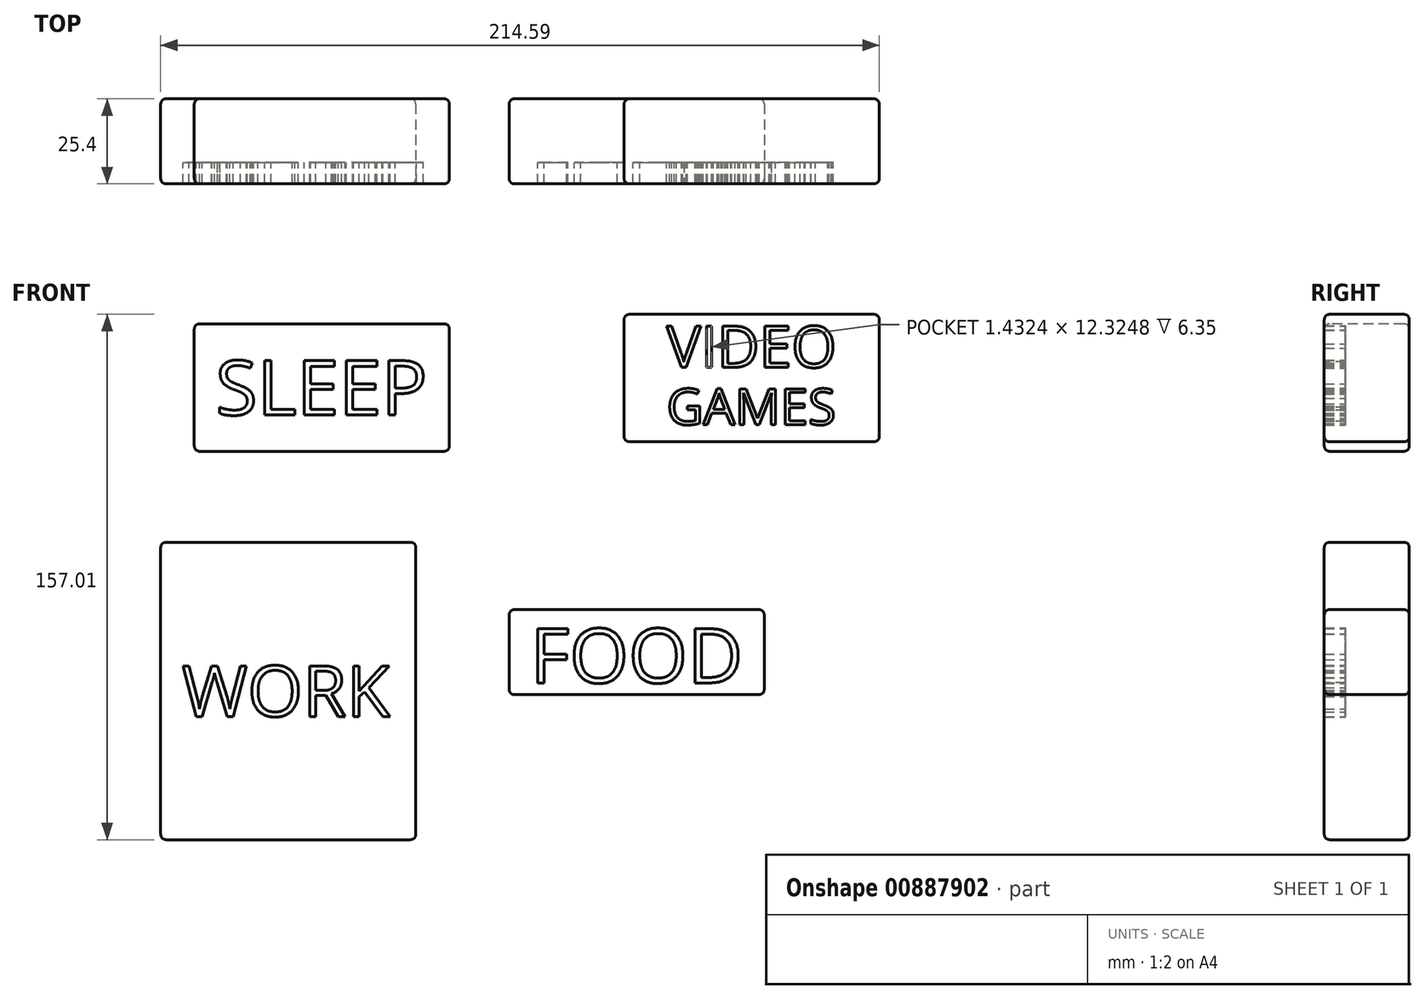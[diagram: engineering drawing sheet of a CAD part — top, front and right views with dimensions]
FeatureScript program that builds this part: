
annotation { "Feature Type Name" : "Feature", "Feature Type Description" : "" }
export const myFeature = defineFeature(function(context is Context, id is Id, definition is map)
    precondition{}
    {
        {
            var Q0;
            Q0=qCreatedBy(makeId("Front.planeOp"),FACE);
            var sketch = newSketch(context, id + "F0", { "sketchPlane" : qUnion([Q0])});
            skLineSegment(sketch, "E0.bottom", {"start": v(-75.08, 32.77) * mm, "end": v(1.12, 32.77) * mm});
            skLineSegment(sketch, "E0.top", {"start": v(-75.08, 70.87) * mm, "end": v(1.12, 70.87) * mm});
            skLineSegment(sketch, "E0.left", {"start": v(-75.08, 32.77) * mm, "end": v(-75.08, 70.87) * mm});
            skLineSegment(sketch, "E0.right", {"start": v(1.12, 32.77) * mm, "end": v(1.12, 70.87) * mm});
            skPoint(sketch, "E0.middle", {"position": v(-36.98, 51.82) * mm});
            skLineSegment(sketch, "E1.bottom", {"start": v(18.93, -39.95) * mm, "end": v(95.13, -39.95) * mm});
            skLineSegment(sketch, "E1.top", {"start": v(18.93, -14.55) * mm, "end": v(95.13, -14.55) * mm});
            skLineSegment(sketch, "E1.left", {"start": v(18.93, -39.95) * mm, "end": v(18.93, -14.55) * mm});
            skLineSegment(sketch, "E1.right", {"start": v(95.13, -39.95) * mm, "end": v(95.13, -14.55) * mm});
            skPoint(sketch, "E1.middle", {"position": v(57.03, -27.25) * mm});
            skLineSegment(sketch, "E2.bottom", {"start": v(-85.11, -83.3) * mm, "end": v(-8.91, -83.3) * mm});
            skLineSegment(sketch, "E2.top", {"start": v(-85.11, 5.6) * mm, "end": v(-8.91, 5.6) * mm});
            skLineSegment(sketch, "E2.left", {"start": v(-85.11, -83.3) * mm, "end": v(-85.11, 5.6) * mm});
            skLineSegment(sketch, "E2.right", {"start": v(-8.91, -83.3) * mm, "end": v(-8.91, 5.6) * mm});
            skPoint(sketch, "E2.middle", {"position": v(-47.01, -38.86) * mm});
            skLineSegment(sketch, "E3.bottom", {"start": v(129.48, 35.6) * mm, "end": v(53.28, 35.6) * mm});
            skLineSegment(sketch, "E3.top", {"start": v(129.48, 73.7) * mm, "end": v(53.28, 73.7) * mm});
            skLineSegment(sketch, "E3.left", {"start": v(129.48, 35.6) * mm, "end": v(129.48, 73.7) * mm});
            skLineSegment(sketch, "E3.right", {"start": v(53.28, 35.6) * mm, "end": v(53.28, 73.7) * mm});
            skPoint(sketch, "E3.middle", {"position": v(91.38, 54.65) * mm});
            skText(sketch, "E4", { "text": "WORK", "fontName": "OpenSans-Regular.ttf"});
            skText(sketch, "E5", { "text": "FOOD", "fontName": "OpenSans-Regular.ttf"});
            skText(sketch, "E6", { "text": "VIDEO", "fontName": "OpenSans-Regular.ttf"});
            skText(sketch, "E7", { "text": "GAMES", "fontName": "OpenSans-Regular.ttf"});
            skText(sketch, "E8", { "text": "SLEEP", "fontName": "OpenSans-Regular.ttf"});
            const initialGuessF0  = {"E4": [-0.07876, -0.04647, 1, 0, 0.01523], "E5": [0.02528, -0.03644, 1, 0, 0.0163], "E6": [0.06598, 0.05782, 1, 0, 0.01243], "E7": [0.06598, 0.04073, 1, 0, 0.0108], "E8": [-0.06873, 0.04364, 1, 0, 0.01635]};
            skSetInitialGuess(sketch, initialGuessF0);
            skSolve(sketch);
        }
        {
            var Q0;
            Q0 = qSketchRegion(id + "F0", true);
            var Q1;
            Q1=makeQuery(id+"F0.imprint","IMPRINT",FACE,{"disambiguationData":[TD([[makeQuery(id+"F0.imprint","IMPRINT",EDGE,{"derivedFrom":sQuery(id+"F0.wireOp",EDGE,"E8.sketch_text.stroke-55")}),-1.0]])]});
            var Q2;
            Q2=makeQuery(id+"F0.imprint","IMPRINT",FACE,{"disambiguationData":[TD([[makeQuery(id+"F0.imprint","IMPRINT",EDGE,{"derivedFrom":sQuery(id+"F0.wireOp",EDGE,"E8.sketch_text.stroke-31")}),-1.0]])]});
            var Q3;
            Q3=makeQuery(id+"F0.imprint","IMPRINT",FACE,{"disambiguationData":[TD([[makeQuery(id+"F0.imprint","IMPRINT",EDGE,{"derivedFrom":sQuery(id+"F0.wireOp",EDGE,"E8.sketch_text.stroke-43")}),-1.0]])]});
            var Q4;
            Q4=makeQuery(id+"F0.imprint","IMPRINT",FACE,{"disambiguationData":[TD([[makeQuery(id+"F0.imprint","IMPRINT",EDGE,{"derivedFrom":sQuery(id+"F0.wireOp",EDGE,"E8.sketch_text.stroke-63")}),1.0]])]});
            var Q5;
            Q5=makeQuery(id+"F0.imprint","IMPRINT",FACE,{"disambiguationData":[TD([[makeQuery(id+"F0.imprint","IMPRINT",EDGE,{"derivedFrom":sQuery(id+"F0.wireOp",EDGE,"E8.sketch_text.stroke-25")}),-1.0]])]});
            var Q6;
            Q6=makeQuery(id+"F0.imprint","IMPRINT",FACE,{"disambiguationData":[TD([[makeQuery(id+"F0.imprint","IMPRINT",EDGE,{"derivedFrom":sQuery(id+"F0.wireOp",EDGE,"E8.sketch_text.stroke-0")}),-1.0]])]});
            var Q7;
            Q7=makeQuery(id+"F0.imprint","IMPRINT",FACE,{"disambiguationData":[TD([[makeQuery(id+"F0.imprint","IMPRINT",EDGE,{"derivedFrom":sQuery(id+"F0.wireOp",EDGE,"E4.sketch_text.stroke-47")}),1.0]])]});
            var Q8;
            Q8=makeQuery(id+"F0.imprint","IMPRINT",FACE,{"disambiguationData":[TD([[makeQuery(id+"F0.imprint","IMPRINT",EDGE,{"derivedFrom":sQuery(id+"F0.wireOp",EDGE,"E4.sketch_text.stroke-36")}),-1.0]])]});
            var Q9;
            Q9=makeQuery(id+"F0.imprint","IMPRINT",FACE,{"disambiguationData":[TD([[makeQuery(id+"F0.imprint","IMPRINT",EDGE,{"derivedFrom":sQuery(id+"F0.wireOp",EDGE,"E4.sketch_text.stroke-54")}),-1.0]])]});
            var Q10;
            Q10=makeQuery(id+"F0.imprint","IMPRINT",FACE,{"disambiguationData":[TD([[makeQuery(id+"F0.imprint","IMPRINT",EDGE,{"derivedFrom":sQuery(id+"F0.wireOp",EDGE,"E4.sketch_text.stroke-20")}),-1.0]])]});
            var Q11;
            Q11=makeQuery(id+"F0.imprint","IMPRINT",FACE,{"disambiguationData":[TD([[makeQuery(id+"F0.imprint","IMPRINT",EDGE,{"derivedFrom":sQuery(id+"F0.wireOp",EDGE,"E4.sketch_text.stroke-28")}),1.0]])]});
            var Q12;
            Q12=makeQuery(id+"F0.imprint","IMPRINT",FACE,{"disambiguationData":[TD([[makeQuery(id+"F0.imprint","IMPRINT",EDGE,{"derivedFrom":sQuery(id+"F0.wireOp",EDGE,"E4.sketch_text.stroke-0")}),-1.0]])]});
            var Q13;
            Q13=makeQuery(id+"F0.imprint","IMPRINT",FACE,{"disambiguationData":[TD([[makeQuery(id+"F0.imprint","IMPRINT",EDGE,{"derivedFrom":sQuery(id+"F0.wireOp",EDGE,"E5.sketch_text.stroke-0")}),-1.0]])]});
            var Q14;
            Q14=makeQuery(id+"F0.imprint","IMPRINT",FACE,{"disambiguationData":[TD([[makeQuery(id+"F0.imprint","IMPRINT",EDGE,{"derivedFrom":sQuery(id+"F0.wireOp",EDGE,"E5.sketch_text.stroke-10")}),-1.0]])]});
            var Q15;
            Q15=makeQuery(id+"F0.imprint","IMPRINT",FACE,{"disambiguationData":[TD([[makeQuery(id+"F0.imprint","IMPRINT",EDGE,{"derivedFrom":sQuery(id+"F0.wireOp",EDGE,"E5.sketch_text.stroke-18")}),1.0]])]});
            var Q16;
            Q16=makeQuery(id+"F0.imprint","IMPRINT",FACE,{"disambiguationData":[TD([[makeQuery(id+"F0.imprint","IMPRINT",EDGE,{"derivedFrom":sQuery(id+"F0.wireOp",EDGE,"E5.sketch_text.stroke-26")}),-1.0]])]});
            var Q17;
            Q17=makeQuery(id+"F0.imprint","IMPRINT",FACE,{"disambiguationData":[TD([[makeQuery(id+"F0.imprint","IMPRINT",EDGE,{"derivedFrom":sQuery(id+"F0.wireOp",EDGE,"E5.sketch_text.stroke-34")}),1.0]])]});
            var Q18;
            Q18=makeQuery(id+"F0.imprint","IMPRINT",FACE,{"disambiguationData":[TD([[makeQuery(id+"F0.imprint","IMPRINT",EDGE,{"derivedFrom":sQuery(id+"F0.wireOp",EDGE,"E5.sketch_text.stroke-42")}),-1.0]])]});
            var Q19;
            Q19=makeQuery(id+"F0.imprint","IMPRINT",FACE,{"disambiguationData":[TD([[makeQuery(id+"F0.imprint","IMPRINT",EDGE,{"derivedFrom":sQuery(id+"F0.wireOp",EDGE,"E5.sketch_text.stroke-49")}),1.0]])]});
            var Q20;
            Q20=makeQuery(id+"F0.imprint","IMPRINT",FACE,{"disambiguationData":[TD([[makeQuery(id+"F0.imprint","IMPRINT",EDGE,{"derivedFrom":sQuery(id+"F0.wireOp",EDGE,"E6.sketch_text.stroke-47")}),1.0]])]});
            var Q21;
            Q21=makeQuery(id+"F0.imprint","IMPRINT",FACE,{"disambiguationData":[TD([[makeQuery(id+"F0.imprint","IMPRINT",EDGE,{"derivedFrom":sQuery(id+"F0.wireOp",EDGE,"E6.sketch_text.stroke-39")}),-1.0]])]});
            var Q22;
            Q22=makeQuery(id+"F0.imprint","IMPRINT",FACE,{"disambiguationData":[TD([[makeQuery(id+"F0.imprint","IMPRINT",EDGE,{"derivedFrom":sQuery(id+"F0.wireOp",EDGE,"E6.sketch_text.stroke-27")}),-1.0]])]});
            var Q23;
            Q23=makeQuery(id+"F0.imprint","IMPRINT",FACE,{"disambiguationData":[TD([[makeQuery(id+"F0.imprint","IMPRINT",EDGE,{"derivedFrom":sQuery(id+"F0.wireOp",EDGE,"E6.sketch_text.stroke-20")}),1.0]])]});
            var Q24;
            Q24=makeQuery(id+"F0.imprint","IMPRINT",FACE,{"disambiguationData":[TD([[makeQuery(id+"F0.imprint","IMPRINT",EDGE,{"derivedFrom":sQuery(id+"F0.wireOp",EDGE,"E6.sketch_text.stroke-13")}),-1.0]])]});
            var Q25;
            Q25=makeQuery(id+"F0.imprint","IMPRINT",FACE,{"disambiguationData":[TD([[makeQuery(id+"F0.imprint","IMPRINT",EDGE,{"derivedFrom":sQuery(id+"F0.wireOp",EDGE,"E6.sketch_text.stroke-9")}),-1.0]])]});
            var Q26;
            Q26=makeQuery(id+"F0.imprint","IMPRINT",FACE,{"disambiguationData":[TD([[makeQuery(id+"F0.imprint","IMPRINT",EDGE,{"derivedFrom":sQuery(id+"F0.wireOp",EDGE,"E6.sketch_text.stroke-0")}),-1.0]])]});
            var Q27;
            Q27=makeQuery(id+"F0.imprint","IMPRINT",FACE,{"disambiguationData":[TD([[makeQuery(id+"F0.imprint","IMPRINT",EDGE,{"derivedFrom":sQuery(id+"F0.wireOp",EDGE,"E7.sketch_text.stroke-28")}),1.0]])]});
            var Q28;
            Q28=makeQuery(id+"F0.imprint","IMPRINT",FACE,{"disambiguationData":[TD([[makeQuery(id+"F0.imprint","IMPRINT",EDGE,{"derivedFrom":sQuery(id+"F0.wireOp",EDGE,"E7.sketch_text.stroke-0")}),-1.0]])]});
            var Q29;
            Q29=makeQuery(id+"F0.imprint","IMPRINT",FACE,{"disambiguationData":[TD([[makeQuery(id+"F0.imprint","IMPRINT",EDGE,{"derivedFrom":sQuery(id+"F0.wireOp",EDGE,"E7.sketch_text.stroke-20")}),-1.0]])]});
            var Q30;
            Q30=makeQuery(id+"F0.imprint","IMPRINT",FACE,{"disambiguationData":[TD([[makeQuery(id+"F0.imprint","IMPRINT",EDGE,{"derivedFrom":sQuery(id+"F0.wireOp",EDGE,"E7.sketch_text.stroke-33")}),-1.0]])]});
            var Q31;
            Q31=makeQuery(id+"F0.imprint","IMPRINT",FACE,{"disambiguationData":[TD([[makeQuery(id+"F0.imprint","IMPRINT",EDGE,{"derivedFrom":sQuery(id+"F0.wireOp",EDGE,"E7.sketch_text.stroke-51")}),-1.0]])]});
            var Q32;
            Q32=makeQuery(id+"F0.imprint","IMPRINT",FACE,{"disambiguationData":[TD([[makeQuery(id+"F0.imprint","IMPRINT",EDGE,{"derivedFrom":sQuery(id+"F0.wireOp",EDGE,"E7.sketch_text.stroke-63")}),-1.0]])]});
            extrude(context, id + "F1", {"entities" : qUnion([Q0, Q1, Q2, Q3, Q4, Q5, Q6, Q7, Q8, Q9, Q10, Q11, Q12, Q13, Q14, Q15, Q16, Q17, Q18, Q19, Q20, Q21, Q22, Q23, Q24, Q25, Q26, Q27, Q28, Q29, Q30, Q31, Q32]), "oppositeDirection" : true, "depth" : 19.05 * mm, "offsetDistance" : 25.4 * mm});
        }
        {
            var Q0;
            Q0=makeQuery(id+"F0.imprint","IMPRINT",FACE,{"disambiguationData":[TD([[makeQuery(id+"F0.imprint","IMPRINT",EDGE,{"derivedFrom":sQuery(id+"F0.wireOp",EDGE,"E0.bottom")}),1.0]])]});
            var Q1;
            Q1=makeQuery(id+"F0.imprint","IMPRINT",FACE,{"disambiguationData":[TD([[makeQuery(id+"F0.imprint","IMPRINT",EDGE,{"derivedFrom":sQuery(id+"F0.wireOp",EDGE,"E2.bottom")}),1.0]])]});
            var Q2;
            Q2=makeQuery(id+"F0.imprint","IMPRINT",FACE,{"disambiguationData":[TD([[makeQuery(id+"F0.imprint","IMPRINT",EDGE,{"derivedFrom":sQuery(id+"F0.wireOp",EDGE,"E1.bottom")}),1.0]])]});
            var Q3;
            Q3=makeQuery(id+"F0.imprint","IMPRINT",FACE,{"disambiguationData":[TD([[makeQuery(id+"F0.imprint","IMPRINT",EDGE,{"derivedFrom":sQuery(id+"F0.wireOp",EDGE,"E3.bottom")}),-1.0]])]});
            var Q4;
            Q4=makeQuery(id+"F0.imprint","IMPRINT",FACE,{"disambiguationData":[TD([[makeQuery(id+"F0.imprint","IMPRINT",EDGE,{"derivedFrom":sQuery(id+"F0.wireOp",EDGE,"E8.sketch_text.stroke-63")}),1.0]])]});
            var Q5;
            Q5=makeQuery(id+"F0.imprint","IMPRINT",FACE,{"disambiguationData":[TD([[makeQuery(id+"F0.imprint","IMPRINT",EDGE,{"derivedFrom":sQuery(id+"F0.wireOp",EDGE,"E4.sketch_text.stroke-28")}),1.0]])]});
            var Q6;
            Q6=makeQuery(id+"F0.imprint","IMPRINT",FACE,{"disambiguationData":[TD([[makeQuery(id+"F0.imprint","IMPRINT",EDGE,{"derivedFrom":sQuery(id+"F0.wireOp",EDGE,"E4.sketch_text.stroke-47")}),1.0]])]});
            var Q7;
            Q7=makeQuery(id+"F0.imprint","IMPRINT",FACE,{"disambiguationData":[TD([[makeQuery(id+"F0.imprint","IMPRINT",EDGE,{"derivedFrom":sQuery(id+"F0.wireOp",EDGE,"E5.sketch_text.stroke-34")}),1.0]])]});
            var Q8;
            Q8=makeQuery(id+"F0.imprint","IMPRINT",FACE,{"disambiguationData":[TD([[makeQuery(id+"F0.imprint","IMPRINT",EDGE,{"derivedFrom":sQuery(id+"F0.wireOp",EDGE,"E5.sketch_text.stroke-18")}),1.0]])]});
            var Q9;
            Q9=makeQuery(id+"F0.imprint","IMPRINT",FACE,{"disambiguationData":[TD([[makeQuery(id+"F0.imprint","IMPRINT",EDGE,{"derivedFrom":sQuery(id+"F0.wireOp",EDGE,"E5.sketch_text.stroke-49")}),1.0]])]});
            var Q10;
            Q10=makeQuery(id+"F0.imprint","IMPRINT",FACE,{"disambiguationData":[TD([[makeQuery(id+"F0.imprint","IMPRINT",EDGE,{"derivedFrom":sQuery(id+"F0.wireOp",EDGE,"E6.sketch_text.stroke-20")}),1.0]])]});
            var Q11;
            Q11=makeQuery(id+"F0.imprint","IMPRINT",FACE,{"disambiguationData":[TD([[makeQuery(id+"F0.imprint","IMPRINT",EDGE,{"derivedFrom":sQuery(id+"F0.wireOp",EDGE,"E6.sketch_text.stroke-47")}),1.0]])]});
            var Q12;
            Q12=makeQuery(id+"F0.imprint","IMPRINT",FACE,{"disambiguationData":[TD([[makeQuery(id+"F0.imprint","IMPRINT",EDGE,{"derivedFrom":sQuery(id+"F0.wireOp",EDGE,"E7.sketch_text.stroke-28")}),1.0]])]});
            extrude(context, id + "F2", {"entities" : qUnion([Q0, Q1, Q2, Q3, Q4, Q5, Q6, Q7, Q8, Q9, Q10, Q11, Q12]), "operationType" : NewBodyOperationType.ADD, "depth" : 6.35 * mm, "offsetDistance" : 25.4 * mm});
        }
        {
            var Q0;
            {var subQ0=sQuery(id+"F0.wireOp",EDGE,"E2.left");Q0=makeQuery(id+"F2.boolean.opBoolean","MERGE",FACE,{"derivedFrom":[makeQuery(id+"F1.opExtrude","SWEPT_FACE",FACE,{"disambiguationData":[OSD([subQ0])]}),makeQuery(id+"F2.opExtrude","SWEPT_FACE",FACE,{"disambiguationData":[OSD([subQ0])]})]});}
            var Q1;
            {var subQ0=sQuery(id+"F0.wireOp",EDGE,"E2.bottom");Q1=makeQuery(id+"F2.boolean.opBoolean","MERGE",FACE,{"derivedFrom":[makeQuery(id+"F1.opExtrude","SWEPT_FACE",FACE,{"disambiguationData":[OSD([subQ0])]}),makeQuery(id+"F2.opExtrude","SWEPT_FACE",FACE,{"disambiguationData":[OSD([subQ0])]})]});}
            var Q2;
            {var subQ0=sQuery(id+"F0.wireOp",EDGE,"E1.bottom");Q2=makeQuery(id+"F2.boolean.opBoolean","MERGE",FACE,{"derivedFrom":[makeQuery(id+"F1.opExtrude","SWEPT_FACE",FACE,{"disambiguationData":[OSD([subQ0])]}),makeQuery(id+"F2.opExtrude","SWEPT_FACE",FACE,{"disambiguationData":[OSD([subQ0])]})]});}
            var Q3;
            {var subQ0=sQuery(id+"F0.wireOp",EDGE,"E3.right");Q3=makeQuery(id+"F2.boolean.opBoolean","MERGE",FACE,{"derivedFrom":[makeQuery(id+"F1.opExtrude","SWEPT_FACE",FACE,{"disambiguationData":[OSD([subQ0])]}),makeQuery(id+"F2.opExtrude","SWEPT_FACE",FACE,{"disambiguationData":[OSD([subQ0])]})]});}
            var Q4;
            {var subQ0=sQuery(id+"F0.wireOp",EDGE,"E3.bottom");Q4=makeQuery(id+"F2.boolean.opBoolean","MERGE",FACE,{"derivedFrom":[makeQuery(id+"F1.opExtrude","SWEPT_FACE",FACE,{"disambiguationData":[OSD([subQ0])]}),makeQuery(id+"F2.opExtrude","SWEPT_FACE",FACE,{"disambiguationData":[OSD([subQ0])]})]});}
            var Q5;
            {var subQ0=sQuery(id+"F0.wireOp",EDGE,"E1.left");Q5=makeQuery(id+"F2.boolean.opBoolean","MERGE",FACE,{"derivedFrom":[makeQuery(id+"F1.opExtrude","SWEPT_FACE",FACE,{"disambiguationData":[OSD([subQ0])]}),makeQuery(id+"F2.opExtrude","SWEPT_FACE",FACE,{"disambiguationData":[OSD([subQ0])]})]});}
            var Q6;
            {var subQ0=sQuery(id+"F0.wireOp",EDGE,"E0.bottom");Q6=makeQuery(id+"F2.boolean.opBoolean","MERGE",FACE,{"derivedFrom":[makeQuery(id+"F1.opExtrude","SWEPT_FACE",FACE,{"disambiguationData":[OSD([subQ0])]}),makeQuery(id+"F2.opExtrude","SWEPT_FACE",FACE,{"disambiguationData":[OSD([subQ0])]})]});}
            var Q7;
            {var subQ0=sQuery(id+"F0.wireOp",EDGE,"E0.left");Q7=makeQuery(id+"F2.boolean.opBoolean","MERGE",FACE,{"derivedFrom":[makeQuery(id+"F1.opExtrude","SWEPT_FACE",FACE,{"disambiguationData":[OSD([subQ0])]}),makeQuery(id+"F2.opExtrude","SWEPT_FACE",FACE,{"disambiguationData":[OSD([subQ0])]})]});}
            var Q8;
            {var subQ0=sQuery(id+"F0.wireOp",EDGE,"E0.top");Q8=makeQuery(id+"F2.boolean.opBoolean","MERGE",FACE,{"derivedFrom":[makeQuery(id+"F1.opExtrude","SWEPT_FACE",FACE,{"disambiguationData":[OSD([subQ0])]}),makeQuery(id+"F2.opExtrude","SWEPT_FACE",FACE,{"disambiguationData":[OSD([subQ0])]})]});}
            var Q9;
            {var subQ0=sQuery(id+"F0.wireOp",EDGE,"E2.top");Q9=makeQuery(id+"F2.boolean.opBoolean","MERGE",FACE,{"derivedFrom":[makeQuery(id+"F1.opExtrude","SWEPT_FACE",FACE,{"disambiguationData":[OSD([subQ0])]}),makeQuery(id+"F2.opExtrude","SWEPT_FACE",FACE,{"disambiguationData":[OSD([subQ0])]})]});}
            var Q10;
            {var subQ0=sQuery(id+"F0.wireOp",EDGE,"E1.top");Q10=makeQuery(id+"F2.boolean.opBoolean","MERGE",FACE,{"derivedFrom":[makeQuery(id+"F1.opExtrude","SWEPT_FACE",FACE,{"disambiguationData":[OSD([subQ0])]}),makeQuery(id+"F2.opExtrude","SWEPT_FACE",FACE,{"disambiguationData":[OSD([subQ0])]})]});}
            var Q11;
            {var subQ0=sQuery(id+"F0.wireOp",EDGE,"E3.top");Q11=makeQuery(id+"F2.boolean.opBoolean","MERGE",FACE,{"derivedFrom":[makeQuery(id+"F1.opExtrude","SWEPT_FACE",FACE,{"disambiguationData":[OSD([subQ0])]}),makeQuery(id+"F2.opExtrude","SWEPT_FACE",FACE,{"disambiguationData":[OSD([subQ0])]})]});}
            var Q12;
            Q12=makeQuery(id+"F1.opExtrude","CAP_FACE",FACE,{"disambiguationData":[OSD([sQuery(id+"F0.wireOp",EDGE,"E0.bottom"),sQuery(id+"F0.wireOp",EDGE,"E0.top"),sQuery(id+"F0.wireOp",EDGE,"E0.left"),sQuery(id+"F0.wireOp",EDGE,"E0.right")])],"isStart":false});
            var Q13;
            Q13=makeQuery(id+"F1.opExtrude","CAP_FACE",FACE,{"disambiguationData":[OSD([sQuery(id+"F0.wireOp",EDGE,"E2.bottom"),sQuery(id+"F0.wireOp",EDGE,"E2.top"),sQuery(id+"F0.wireOp",EDGE,"E2.left"),sQuery(id+"F0.wireOp",EDGE,"E2.right")])],"isStart":false});
            var Q14;
            Q14=makeQuery(id+"F1.opExtrude","CAP_FACE",FACE,{"disambiguationData":[OSD([sQuery(id+"F0.wireOp",EDGE,"E1.bottom"),sQuery(id+"F0.wireOp",EDGE,"E1.top"),sQuery(id+"F0.wireOp",EDGE,"E1.left"),sQuery(id+"F0.wireOp",EDGE,"E1.right")])],"isStart":false});
            var Q15;
            {var subQ0=sQuery(id+"F0.wireOp",EDGE,"E0.right");Q15=makeQuery(id+"F2.boolean.opBoolean","MERGE",FACE,{"derivedFrom":[makeQuery(id+"F1.opExtrude","SWEPT_FACE",FACE,{"disambiguationData":[OSD([subQ0])]}),makeQuery(id+"F2.opExtrude","SWEPT_FACE",FACE,{"disambiguationData":[OSD([subQ0])]})]});}
            var Q16;
            {var subQ0=sQuery(id+"F0.wireOp",EDGE,"E3.left");Q16=makeQuery(id+"F2.boolean.opBoolean","MERGE",FACE,{"derivedFrom":[makeQuery(id+"F1.opExtrude","SWEPT_FACE",FACE,{"disambiguationData":[OSD([subQ0])]}),makeQuery(id+"F2.opExtrude","SWEPT_FACE",FACE,{"disambiguationData":[OSD([subQ0])]})]});}
            var Q17;
            {var subQ0=sQuery(id+"F0.wireOp",EDGE,"E2.right");Q17=makeQuery(id+"F2.boolean.opBoolean","MERGE",FACE,{"derivedFrom":[makeQuery(id+"F1.opExtrude","SWEPT_FACE",FACE,{"disambiguationData":[OSD([subQ0])]}),makeQuery(id+"F2.opExtrude","SWEPT_FACE",FACE,{"disambiguationData":[OSD([subQ0])]})]});}
            var Q18;
            {var subQ0=sQuery(id+"F0.wireOp",EDGE,"E1.right");Q18=makeQuery(id+"F2.boolean.opBoolean","MERGE",FACE,{"derivedFrom":[makeQuery(id+"F1.opExtrude","SWEPT_FACE",FACE,{"disambiguationData":[OSD([subQ0])]}),makeQuery(id+"F2.opExtrude","SWEPT_FACE",FACE,{"disambiguationData":[OSD([subQ0])]})]});}
            fillet(context, id + "F3", {"entities" : qUnion([Q0, Q1, Q2, Q3, Q4, Q5, Q6, Q7, Q8, Q9, Q10, Q11, Q12, Q13, Q14, Q15, Q16, Q17, Q18]), "radius" : 1.59 * mm, "tangentPropagation" : true, "allowEdgeOverflow" : false});
        }
    });
